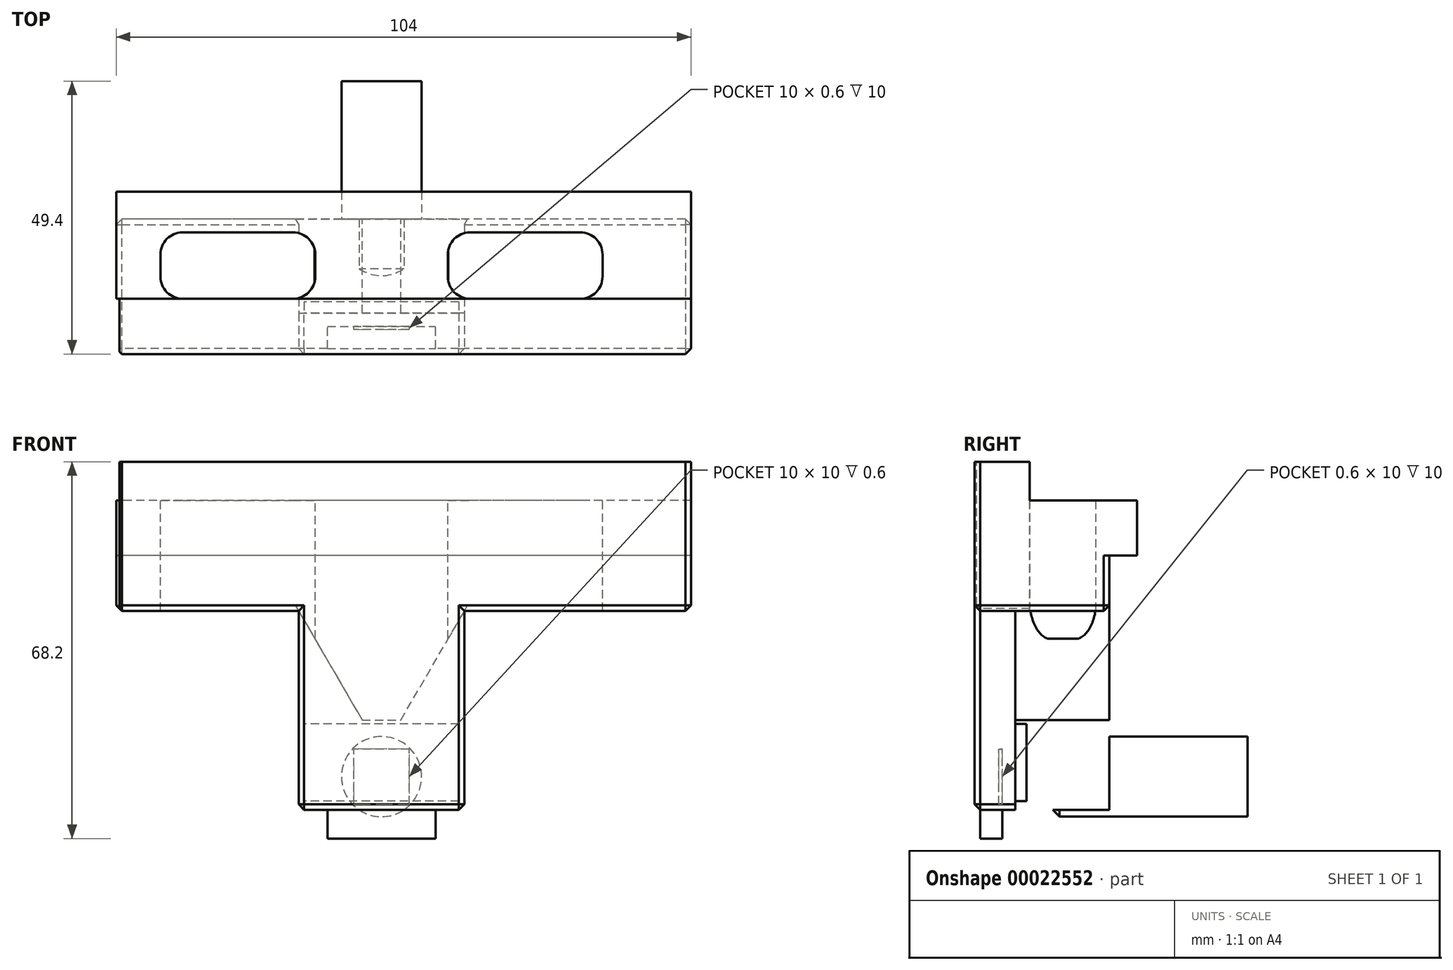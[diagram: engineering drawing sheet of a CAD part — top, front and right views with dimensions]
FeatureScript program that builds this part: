
annotation { "Feature Type Name" : "Feature", "Feature Type Description" : "" }
export const myFeature = defineFeature(function(context is Context, id is Id, definition is map)
    precondition{}
    {
        {
            var Q0;
            Q0=qCreatedBy(makeId("Top.planeOp"),FACE);
            var sketch = newSketch(context, id + "F0", { "sketchPlane" : qUnion([Q0])});
            skLineSegment(sketch, "E0.rect.bottom", {"start": v(9.8, 2) * mm, "end": v(-9.8, 2) * mm});
            skLineSegment(sketch, "E0.rect.top", {"start": v(9.8, -2) * mm, "end": v(-9.8, -2) * mm});
            skLineSegment(sketch, "E0.rect.left", {"start": v(9.8, 2) * mm, "end": v(9.8, -2) * mm});
            skLineSegment(sketch, "E0.rect.right", {"start": v(-9.8, 2) * mm, "end": v(-9.8, -2) * mm});
            skPoint(sketch, "E0.rect.middle", {"position": v(0, 0) * mm});
            skSolve(sketch);
        }
        {
            var Q0;
            Q0=qSketchRegion(id+"F0",true);
            extrude(context, id + "F1", {"entities" : qUnion([Q0]), "depth" : 65 * mm});
        }
        {
            var Q0;
            Q0=makeQuery(id+"F1.opExtrude","SWEPT_FACE",FACE,{"disambiguationData":[OSD([sQuery(id+"F0.wireOp",EDGE,"E0.rect.bottom")])]});
            var sketch = newSketch(context, id + "F2", { "sketchPlane" : qUnion([Q0])});
            skLineSegment(sketch, "E1.rect.bottom", {"start": v(-5, 64.8) * mm, "end": v(5, 64.8) * mm});
            skLineSegment(sketch, "E1.rect.top", {"start": v(-5, 35) * mm, "end": v(5, 35) * mm});
            skLineSegment(sketch, "E1.rect.left", {"start": v(-5, 64.8) * mm, "end": v(-5, 35) * mm});
            skLineSegment(sketch, "E1.rect.right", {"start": v(5, 64.8) * mm, "end": v(5, 35) * mm});
            skPoint(sketch, "E1.rect.middle", {"position": v(0, 49.9) * mm});
            skSolve(sketch);
        }
        {
            var Q0;
            Q0=qSketchRegion(id+"F2",true);
            extrude(context, id + "F3", {"entities" : qUnion([Q0]), "operationType" : NewBodyOperationType.ADD, "depth" : 1 * mm});
        }
        {
            var Q0;
            Q0=makeQuery(id+"F3.opExtrude","SWEPT_EDGE",EDGE,{"disambiguationData":[OSD([sQuery(id+"F2.wireOp",EDGE,"E1.rect.top"),sQuery(id+"F2.wireOp",EDGE,"E1.rect.left")])]});
            var Q1;
            Q1=makeQuery(id+"F3.opExtrude","SWEPT_EDGE",EDGE,{"disambiguationData":[OSD([sQuery(id+"F2.wireOp",EDGE,"E1.rect.top"),sQuery(id+"F2.wireOp",EDGE,"E1.rect.right")])]});
            var Q2;
            Q2=makeQuery(id+"F3.opExtrude","SWEPT_EDGE",EDGE,{"disambiguationData":[OSD([sQuery(id+"F2.wireOp",EDGE,"E1.rect.bottom"),sQuery(id+"F2.wireOp",EDGE,"E1.rect.left")])]});
            var Q3;
            Q3=makeQuery(id+"F3.opExtrude","SWEPT_EDGE",EDGE,{"disambiguationData":[OSD([sQuery(id+"F2.wireOp",EDGE,"E1.rect.bottom"),sQuery(id+"F2.wireOp",EDGE,"E1.rect.right")])]});
            fillet(context, id + "F4", {"entities" : qUnion([Q0, Q1, Q2, Q3]), "radius" : 5 * mm, "tangentPropagation" : true, "allowEdgeOverflow" : false});
        }
        {
            var Q0;
            Q0=qCreatedBy(makeId("Top.planeOp"),FACE);
            cPlane(context, id + "F5", {"entities" : qUnion([Q0]), "cplaneType" : CPlaneType.OFFSET, "offset" : 11.2 * mm, "width" : 150 * mm, "height" : 150 * mm});
        }
        {
            var Q0;
            Q0=qCreatedBy(id+"F5.planeOp",FACE);
            cPlane(context, id + "F6", {"entities" : qUnion([Q0]), "cplaneType" : CPlaneType.OFFSET, "offset" : 40 * mm, "width" : 150 * mm, "height" : 150 * mm});
        }
        {
            var Q0;
            Q0=qCreatedBy(makeId("Right.planeOp"),FACE);
            var sketch = newSketch(context, id + "F7", { "sketchPlane" : qUnion([Q0])});
            skLineSegment(sketch, "E2", {"start": v(-3, 68.2) * mm, "end": v(-3, 41.2) * mm});
            skLineSegment(sketch, "E3", {"start": v(-3, 41.2) * mm, "end": v(21.4, 41.2) * mm});
            skLineSegment(sketch, "E4", {"start": v(21.4, 41.2) * mm, "end": v(21.4, 51.2) * mm});
            skLineSegment(sketch, "E5", {"start": v(21.4, 51.2) * mm, "end": v(26.4, 51.2) * mm});
            skLineSegment(sketch, "E6", {"start": v(26.4, 51.2) * mm, "end": v(26.4, 61.2) * mm});
            skLineSegment(sketch, "E7", {"start": v(26.4, 61.2) * mm, "end": v(7, 61.2) * mm});
            skLineSegment(sketch, "E8", {"start": v(7, 61.2) * mm, "end": v(7, 68.2) * mm});
            skLineSegment(sketch, "E9", {"start": v(7, 68.2) * mm, "end": v(-3, 68.2) * mm});
            skSolve(sketch);
        }
        {
            var Q0;
            Q0=qSketchRegion(id+"F7",true);
            extrude(context, id + "F8", {"entities" : qUnion([Q0]), "depth" : (104 - 48) * mm, "hasSecondDirection" : true, "secondDirectionOppositeDirection" : true, "secondDirectionDepth" : 48 * mm});
        }
        {
            var Q0;
            Q0=makeQuery(id+"F8.opExtrude","SWEPT_FACE",FACE,{"disambiguationData":[OSD([sQuery(id+"F7.wireOp",EDGE,"E3")])]});
            var sketch = newSketch(context, id + "F9", { "sketchPlane" : qUnion([Q0])});
            skLineSegment(sketch, "E10", {"start": v(0, -21.4) * mm, "end": v(0, 3) * mm});
            skLineSegment(sketch, "E11.rect.bottom", {"start": v(-15, -21.4) * mm, "end": v(15, -21.4) * mm});
            skLineSegment(sketch, "E11.rect.top", {"start": v(-15, 3) * mm, "end": v(15, 3) * mm});
            skLineSegment(sketch, "E11.rect.left", {"start": v(-15, -21.4) * mm, "end": v(-15, 3) * mm});
            skLineSegment(sketch, "E11.rect.right", {"start": v(15, -21.4) * mm, "end": v(15, 3) * mm});
            skPoint(sketch, "E11.rect.middle", {"position": v(0, -9.2) * mm});
            skSolve(sketch);
        }
        {
            var Q0;
            Q0=qSketchRegion(id+"F9",true);
            extrude(context, id + "F10", {"entities" : qUnion([Q0]), "operationType" : NewBodyOperationType.ADD, "depth" : 36 * mm});
        }
        {
            var Q0;
            Q0=makeQuery(id+"F8.opExtrude","SWEPT_FACE",FACE,{"disambiguationData":[OSD([sQuery(id+"F7.wireOp",EDGE,"E7")])]});
            var sketch = newSketch(context, id + "F11", { "sketchPlane" : qUnion([Q0])});
            skLineSegment(sketch, "E12.rect.bottom", {"start": v(-36, 19) * mm, "end": v(-16, 19) * mm});
            skLineSegment(sketch, "E12.rect.top", {"start": v(-36, 7) * mm, "end": v(-16, 7) * mm});
            skLineSegment(sketch, "E12.rect.left", {"start": v(-40, 15) * mm, "end": v(-40, 11) * mm});
            skLineSegment(sketch, "E12.rect.right", {"start": v(-12, 15) * mm, "end": v(-12, 11) * mm});
            skPoint(sketch, "E12.rect.middle", {"position": v(-26, 13) * mm});
            skPoint(sketch, "E13.visualSharp", {"position": v(-40, 19) * mm});
            skArc(sketch, "E13.filletArc", {"start": v(-36, 19) * mm, "mid": v(-38.83, 17.83) * mm, "end": v(-40, 15) * mm});
            skPoint(sketch, "E14.visualSharp", {"position": v(-12, 19) * mm});
            skArc(sketch, "E14.filletArc", {"start": v(-12, 15) * mm, "mid": v(-13.17, 17.83) * mm, "end": v(-16, 19) * mm});
            skPoint(sketch, "E15.visualSharp", {"position": v(-12, 7) * mm});
            skArc(sketch, "E15.filletArc", {"start": v(-16, 7) * mm, "mid": v(-13.17, 8.17) * mm, "end": v(-12, 11) * mm});
            skPoint(sketch, "E16.visualSharp", {"position": v(-40, 7) * mm});
            skArc(sketch, "E16.filletArc", {"start": v(-40, 11) * mm, "mid": v(-38.83, 8.17) * mm, "end": v(-36, 7) * mm});
            skLineSegment(sketch, "E17.MirrorCS", {"start": v(40, 15) * mm, "end": v(40, 11) * mm});
            skPoint(sketch, "E18.MirrorP", {"position": v(12, 7) * mm});
            skArc(sketch, "E19.MirrorCS", {"start": v(16, 7) * mm, "mid": v(13.17, 8.17) * mm, "end": v(12, 11) * mm});
            skLineSegment(sketch, "E20.MirrorCS", {"start": v(12, 15) * mm, "end": v(12, 11) * mm});
            skPoint(sketch, "E21.MirrorP", {"position": v(26, 13) * mm});
            skPoint(sketch, "E22.MirrorP", {"position": v(40, 19) * mm});
            skLineSegment(sketch, "E23.MirrorCS", {"start": v(36, 19) * mm, "end": v(16, 19) * mm});
            skPoint(sketch, "E24.MirrorP", {"position": v(40, 7) * mm});
            skPoint(sketch, "E25.MirrorP", {"position": v(12, 19) * mm});
            skArc(sketch, "E26.MirrorCS", {"start": v(40, 11) * mm, "mid": v(38.83, 8.17) * mm, "end": v(36, 7) * mm});
            skArc(sketch, "E27.MirrorCS", {"start": v(36, 19) * mm, "mid": v(38.83, 17.83) * mm, "end": v(40, 15) * mm});
            skArc(sketch, "E28.MirrorCS", {"start": v(12, 15) * mm, "mid": v(13.17, 17.83) * mm, "end": v(16, 19) * mm});
            skLineSegment(sketch, "E29.MirrorCS", {"start": v(36, 7) * mm, "end": v(16, 7) * mm});
            skSolve(sketch);
        }
        {
            var Q0;
            Q0=qSketchRegion(id+"F11",true);
            extrude(context, id + "F12", {"entities" : qUnion([Q0]), "operationType" : NewBodyOperationType.REMOVE, "oppositeDirection" : true, "depth" : 25 * mm});
        }
        {
            var Q0;
            Q0=makeQuery(id+"F2.imprint","IMPRINT",FACE,{"disambiguationData":[TD([[makeQuery(id+"F2.imprint","IMPRINT",EDGE,{"derivedFrom":sQuery(id+"F2.wireOp",EDGE,"E1.rect.bottom")}),1.0]])]});
            var sketch = newSketch(context, id + "F13", { "sketchPlane" : qUnion([Q0])});
            skLineSegment(sketch, "E30.rect.bottom", {"start": v(-5, 6.2) * mm, "end": v(5, 6.2) * mm});
            skLineSegment(sketch, "E30.rect.top", {"start": v(-5, 16.2) * mm, "end": v(5, 16.2) * mm});
            skLineSegment(sketch, "E30.rect.left", {"start": v(-5, 6.2) * mm, "end": v(-5, 16.2) * mm});
            skLineSegment(sketch, "E30.rect.right", {"start": v(5, 6.2) * mm, "end": v(5, 16.2) * mm});
            skPoint(sketch, "E30.rect.middle", {"position": v(0, 11.2) * mm});
            skSolve(sketch);
        }
        {
            var Q0;
            Q0=qSketchRegion(id+"F13",true);
            extrude(context, id + "F14", {"entities" : qUnion([Q0]), "operationType" : NewBodyOperationType.REMOVE, "oppositeDirection" : true, "depth" : .6 * mm});
        }
        {
            var Q0;
            Q0=makeQuery(id+"F10.boolean.opBoolean","MERGE",FACE,{"derivedFrom":[makeQuery(id+"F8.opExtrude","SWEPT_FACE",FACE,{"disambiguationData":[OSD([sQuery(id+"F7.wireOp",EDGE,"E4")])]}),makeQuery(id+"F10.opExtrude","SWEPT_FACE",FACE,{"disambiguationData":[OSD([sQuery(id+"F9.wireOp",EDGE,"E11.rect.bottom")])]})]});
            var sketch = newSketch(context, id + "F15", { "sketchPlane" : qUnion([Q0])});
            skCircle(sketch, "E31", {"center": v(0, 11.2) * mm, "radius": 7.25 * mm});
            skSolve(sketch);
        }
        {
            var Q0;
            Q0=qSketchRegion(id+"F15",true);
            extrude(context, id + "F16", {"entities" : qUnion([Q0]), "operationType" : NewBodyOperationType.ADD, "depth" : 25 * mm, "hasSecondDirection" : true, "secondDirectionOppositeDirection" : true, "secondDirectionDepth" : (25.4 - 11.4) * mm});
        }
        {
            var Q0;
            Q0=makeQuery(id+"F16.opExtrude","CAP_EDGE",EDGE,{"disambiguationData":[OSD([sQuery(id+"F15.wireOp",EDGE,"E31")])],"isStart":true});
            chamfer(context, id + "F17", {"entities" : qUnion([Q0]), "width" : 5 * mm, "tangentPropagation" : true});
        }
        {
            var Q0;
            Q0=makeQuery(id+"F8.opExtrude","SWEPT_FACE",FACE,{"disambiguationData":[OSD([sQuery(id+"F7.wireOp",EDGE,"E9")])]});
            var sketch = newSketch(context, id + "F18", { "sketchPlane" : qUnion([Q0])});
            skLineSegment(sketch, "E32.rect.bottom", {"start": v(9.9, -2) * mm, "end": v(-9.9, -2) * mm});
            skLineSegment(sketch, "E32.rect.top", {"start": v(9.9, 2.8) * mm, "end": v(-9.9, 2.8) * mm});
            skLineSegment(sketch, "E32.rect.left", {"start": v(9.9, -2) * mm, "end": v(9.9, 2.8) * mm});
            skLineSegment(sketch, "E32.rect.right", {"start": v(-9.9, -2) * mm, "end": v(-9.9, 2.8) * mm});
            skPoint(sketch, "E32.rect.middle", {"position": v(0, 0.4) * mm});
            skSolve(sketch);
        }
        {
            var Q0;
            Q0=makeQuery(id+"F10.boolean.opBoolean","MERGE",FACE,{"derivedFrom":[makeQuery(id+"F8.opExtrude","SWEPT_FACE",FACE,{"disambiguationData":[OSD([sQuery(id+"F7.wireOp",EDGE,"E4")])]}),makeQuery(id+"F10.opExtrude","SWEPT_FACE",FACE,{"disambiguationData":[OSD([sQuery(id+"F9.wireOp",EDGE,"E11.rect.bottom")])]})]});
            var sketch = newSketch(context, id + "F19", { "sketchPlane" : qUnion([Q0])});
            skLineSegment(sketch, "E33", {"start": v(-15, 41.2) * mm, "end": v(-15, 5.2) * mm});
            skLineSegment(sketch, "E34", {"start": v(-15, 5.2) * mm, "end": v(15, 5.2) * mm});
            skLineSegment(sketch, "E35", {"start": v(15, 5.2) * mm, "end": v(15, 41.2) * mm});
            skLineSegment(sketch, "E36", {"start": v(15, 41.2) * mm, "end": v(3.5, 21.45) * mm});
            skLineSegment(sketch, "E37", {"start": v(3.5, 21.45) * mm, "end": v(-3.5, 21.45) * mm});
            skLineSegment(sketch, "E38", {"start": v(-3.5, 21.45) * mm, "end": v(-15, 41.2) * mm});
            skSolve(sketch);
        }
        {
            var Q0;
            Q0=qSketchRegion(id+"F19",true);
            extrude(context, id + "F20", {"entities" : qUnion([Q0]), "operationType" : NewBodyOperationType.REMOVE, "oppositeDirection" : true, "depth" : 17 * mm});
        }
        {
            var Q0;
            {var subQ0=sQuery(id+"F7.wireOp",EDGE,"E3");var subQ1=sQuery(id+"F7.wireOp",EDGE,"E4");Q0=makeQuery(id+"F10.boolean.opBoolean","SPLIT",EDGE,{"disambiguationData":[TD([makeQuery(id+"F10.opExtrude","SWEPT_FACE",FACE,{"disambiguationData":[OSD([sQuery(id+"F9.wireOp",EDGE,"E11.rect.right")])]})])],"derivedFrom":makeQuery(id+"F8.opExtrude","SWEPT_EDGE",EDGE,{"disambiguationData":[OSD([subQ0,subQ1])]})});}
            var Q1;
            Q1=makeQuery(id+"F8.opExtrude","CAP_EDGE",EDGE,{"disambiguationData":[OSD([sQuery(id+"F7.wireOp",EDGE,"E3")])],"isStart":false});
            var Q2;
            {var subQ0=sQuery(id+"F7.wireOp",EDGE,"E2");var subQ1=sQuery(id+"F7.wireOp",EDGE,"E3");Q2=makeQuery(id+"F10.boolean.opBoolean","SPLIT",EDGE,{"disambiguationData":[TD([makeQuery(id+"F10.opExtrude","SWEPT_FACE",FACE,{"disambiguationData":[OSD([sQuery(id+"F9.wireOp",EDGE,"E11.rect.right")])]})])],"derivedFrom":makeQuery(id+"F8.opExtrude","SWEPT_EDGE",EDGE,{"disambiguationData":[OSD([subQ0,subQ1])]})});}
            var Q3;
            Q3=makeQuery(id+"F20.boolean.opBoolean","COPY",EDGE,{"derivedFrom":makeQuery(id+"F20.opExtrude","CAP_EDGE",EDGE,{"disambiguationData":[OSD([sQuery(id+"F19.wireOp",EDGE,"4e5723cc-c56b-4f50-8f02-6089d21b5447")])],"isStart":true})});
            var Q4;
            Q4=makeQuery(id+"F10.opExtrude","SWEPT_EDGE",EDGE,{"disambiguationData":[OSD([sQuery(id+"F7.wireOp",EDGE,"E2"),sQuery(id+"F7.wireOp",EDGE,"E3"),sQuery(id+"F9.wireOp",EDGE,"E11.rect.top"),sQuery(id+"F9.wireOp",EDGE,"E11.rect.right")])]});
            var Q5;
            Q5=makeQuery(id+"F20.boolean.opBoolean","COPY",EDGE,{"derivedFrom":makeQuery(id+"F20.opExtrude","CAP_EDGE",EDGE,{"disambiguationData":[OSD([sQuery(id+"F19.wireOp",EDGE,"e59e6528-5edc-417b-ab9c-6e33f9ba458c")])],"isStart":false})});
            var Q6;
            Q6=makeQuery(id+"F20.boolean.opBoolean","COPY",EDGE,{"derivedFrom":makeQuery(id+"F20.opExtrude","CAP_EDGE",EDGE,{"disambiguationData":[OSD([sQuery(id+"F19.wireOp",EDGE,"1b5662a8-ce83-4df6-836d-e45ffbacdfc2")])],"isStart":false})});
            var Q7;
            Q7=makeQuery(id+"F10.opExtrude","CAP_EDGE",EDGE,{"disambiguationData":[OSD([sQuery(id+"F9.wireOp",EDGE,"E11.rect.right")])],"isStart":false});
            var Q8;
            Q8=makeQuery(id+"F10.opExtrude","CAP_EDGE",EDGE,{"disambiguationData":[OSD([sQuery(id+"F9.wireOp",EDGE,"E11.rect.top")])],"isStart":false});
            var Q9;
            Q9=makeQuery(id+"F20.boolean.opBoolean","COPY",EDGE,{"derivedFrom":makeQuery(id+"F20.opExtrude","CAP_EDGE",EDGE,{"disambiguationData":[OSD([sQuery(id+"F19.wireOp",EDGE,"000c07ea-096d-4c4e-9cd7-be6bbeb4396f")])],"isStart":true})});
            var Q10;
            Q10=makeQuery(id+"F10.opExtrude","CAP_EDGE",EDGE,{"disambiguationData":[OSD([sQuery(id+"F9.wireOp",EDGE,"E11.rect.bottom")])],"isStart":false});
            var Q11;
            {var subQ0=sQuery(id+"F7.wireOp",EDGE,"E3");var subQ1=sQuery(id+"F7.wireOp",EDGE,"E4");Q11=makeQuery(id+"F10.boolean.opBoolean","SPLIT",EDGE,{"disambiguationData":[TD([makeQuery(id+"F10.opExtrude","SWEPT_FACE",FACE,{"disambiguationData":[OSD([sQuery(id+"F9.wireOp",EDGE,"E11.rect.left")])]})])],"derivedFrom":makeQuery(id+"F8.opExtrude","SWEPT_EDGE",EDGE,{"disambiguationData":[OSD([subQ0,subQ1])]})});}
            var Q12;
            Q12=makeQuery(id+"F8.opExtrude","CAP_EDGE",EDGE,{"disambiguationData":[OSD([sQuery(id+"F7.wireOp",EDGE,"E3")])],"isStart":true});
            var Q13;
            {var subQ0=sQuery(id+"F7.wireOp",EDGE,"E2");var subQ1=sQuery(id+"F7.wireOp",EDGE,"E3");Q13=makeQuery(id+"F10.boolean.opBoolean","SPLIT",EDGE,{"disambiguationData":[TD([makeQuery(id+"F10.opExtrude","SWEPT_FACE",FACE,{"disambiguationData":[OSD([sQuery(id+"F9.wireOp",EDGE,"E11.rect.left")])]})])],"derivedFrom":makeQuery(id+"F8.opExtrude","SWEPT_EDGE",EDGE,{"disambiguationData":[OSD([subQ0,subQ1])]})});}
            var Q14;
            Q14=makeQuery(id+"F16.opExtrude","SWEPT_FACE",FACE,{"disambiguationData":[OSD([sQuery(id+"F15.wireOp",EDGE,"E31")])]});
            var Q15;
            Q15=makeQuery(id+"F20.boolean.opBoolean","COPY",EDGE,{"derivedFrom":makeQuery(id+"F20.opExtrude","CAP_EDGE",EDGE,{"disambiguationData":[OSD([sQuery(id+"F19.wireOp",EDGE,"9e232a22-7e64-44e9-a8b5-7caafe2406f6")])],"isStart":false})});
            var Q16;
            Q16=makeQuery(id+"F10.opExtrude","CAP_EDGE",EDGE,{"disambiguationData":[OSD([sQuery(id+"F9.wireOp",EDGE,"E11.rect.left")])],"isStart":false});
            var Q17;
            Q17=makeQuery(id+"F8.opExtrude","CAP_EDGE",EDGE,{"disambiguationData":[OSD([sQuery(id+"F7.wireOp",EDGE,"E2")])],"isStart":true});
            var Q18;
            Q18=makeQuery(id+"F8.opExtrude","CAP_EDGE",EDGE,{"disambiguationData":[OSD([sQuery(id+"F7.wireOp",EDGE,"E4")])],"isStart":true});
            var Q19;
            Q19=makeQuery(id+"F8.opExtrude","CAP_EDGE",EDGE,{"disambiguationData":[OSD([sQuery(id+"F7.wireOp",EDGE,"E4")])],"isStart":false});
            var Q20;
            Q20=makeQuery(id+"F8.opExtrude","CAP_EDGE",EDGE,{"disambiguationData":[OSD([sQuery(id+"F7.wireOp",EDGE,"E2")])],"isStart":false});
            var Q21;
            Q21=makeQuery(id+"F20.boolean.opBoolean","COPY",EDGE,{"derivedFrom":makeQuery(id+"F20.opExtrude","CAP_EDGE",EDGE,{"disambiguationData":[OSD([sQuery(id+"F19.wireOp",EDGE,"E38")])],"isStart":true})});
            var Q22;
            Q22=makeQuery(id+"F20.boolean.opBoolean","COPY",EDGE,{"derivedFrom":makeQuery(id+"F20.opExtrude","CAP_EDGE",EDGE,{"disambiguationData":[OSD([sQuery(id+"F19.wireOp",EDGE,"E37")])],"isStart":true})});
            var Q23;
            Q23=makeQuery(id+"F20.boolean.opBoolean","COPY",EDGE,{"derivedFrom":makeQuery(id+"F20.opExtrude","CAP_EDGE",EDGE,{"disambiguationData":[OSD([sQuery(id+"F19.wireOp",EDGE,"E34")])],"isStart":false})});
            var Q24;
            Q24=makeQuery(id+"F20.boolean.opBoolean","COPY",EDGE,{"derivedFrom":makeQuery(id+"F20.opExtrude","CAP_EDGE",EDGE,{"disambiguationData":[OSD([sQuery(id+"F19.wireOp",EDGE,"E36")])],"isStart":true})});
            var Q25;
            Q25=makeQuery(id+"F10.opExtrude","SWEPT_EDGE",EDGE,{"disambiguationData":[OSD([sQuery(id+"F7.wireOp",EDGE,"E2"),sQuery(id+"F7.wireOp",EDGE,"E3"),sQuery(id+"F9.wireOp",EDGE,"E11.rect.top"),sQuery(id+"F9.wireOp",EDGE,"E11.rect.left")])]});
            chamfer(context, id + "F21", {"entities" : qUnion([Q0, Q1, Q2, Q3, Q4, Q5, Q6, Q7, Q8, Q9, Q10, Q11, Q12, Q13, Q14, Q15, Q16, Q17, Q18, Q19, Q20, Q21, Q22, Q23, Q24, Q25]), "width" : 1 * mm, "tangentPropagation" : true});
        }
        {
            var Q0;
            Q0=makeQuery(id+"F20.boolean.opBoolean","COPY",FACE,{"derivedFrom":makeQuery(id+"F20.opExtrude","CAP_FACE",FACE,{"disambiguationData":[OSD([sQuery(id+"F19.wireOp",EDGE,"E33"),sQuery(id+"F19.wireOp",EDGE,"E34"),sQuery(id+"F19.wireOp",EDGE,"E35"),sQuery(id+"F19.wireOp",EDGE,"E36"),sQuery(id+"F19.wireOp",EDGE,"E37"),sQuery(id+"F19.wireOp",EDGE,"E38")])],"isStart":false})});
            var sketch = newSketch(context, id + "F22", { "sketchPlane" : qUnion([Q0])});
            skLineSegment(sketch, "E39.rect.bottom", {"start": v(-14, 6.76) * mm, "end": v(14, 6.76) * mm});
            skLineSegment(sketch, "E39.rect.top", {"start": v(-14, 20.76) * mm, "end": v(14, 20.76) * mm});
            skLineSegment(sketch, "E39.rect.left", {"start": v(-14, 6.76) * mm, "end": v(-14, 20.76) * mm});
            skLineSegment(sketch, "E39.rect.right", {"start": v(14, 6.76) * mm, "end": v(14, 20.76) * mm});
            skPoint(sketch, "E39.rect.middle", {"position": v(0, 13.76) * mm});
            skSolve(sketch);
        }
        {
            var Q0;
            Q0 = qSketchRegion(id + "F22", true);
            extrude(context, id + "F23", {"entities" : qUnion([Q0]), "depth" : 2 * mm});
        }
        {
            var Q0;
            Q0=makeQuery(id+"F8.opExtrude","CAP_FACE",FACE,{"disambiguationData":[OSD([sQuery(id+"F7.wireOp",EDGE,"E2"),sQuery(id+"F7.wireOp",EDGE,"E3"),sQuery(id+"F7.wireOp",EDGE,"E4"),sQuery(id+"F7.wireOp",EDGE,"E5"),sQuery(id+"F7.wireOp",EDGE,"E6"),sQuery(id+"F7.wireOp",EDGE,"E7"),sQuery(id+"F7.wireOp",EDGE,"E8"),sQuery(id+"F7.wireOp",EDGE,"E9")])],"isStart":true});
            var sketch = newSketch(context, id + "F24", { "sketchPlane" : qUnion([Q0])});
            skLineSegment(sketch, "E40.bottom", {"start": v(-7, 68.2) * mm, "end": v(6.93, 68.2) * mm});
            skLineSegment(sketch, "E40.top", {"start": v(-7, 39.08) * mm, "end": v(6.93, 39.08) * mm});
            skLineSegment(sketch, "E40.left", {"start": v(-7, 68.2) * mm, "end": v(-7, 39.08) * mm});
            skLineSegment(sketch, "E40.right", {"start": v(6.93, 68.2) * mm, "end": v(6.93, 39.08) * mm});
            skSolve(sketch);
        }
        {
            var Q0;
            Q0 = qSketchRegion(id + "F24", true);
            extrude(context, id + "F25", {"entities" : qUnion([Q0]), "operationType" : NewBodyOperationType.REMOVE, "oppositeDirection" : true, "depth" : .6 * mm});
        }
    });
